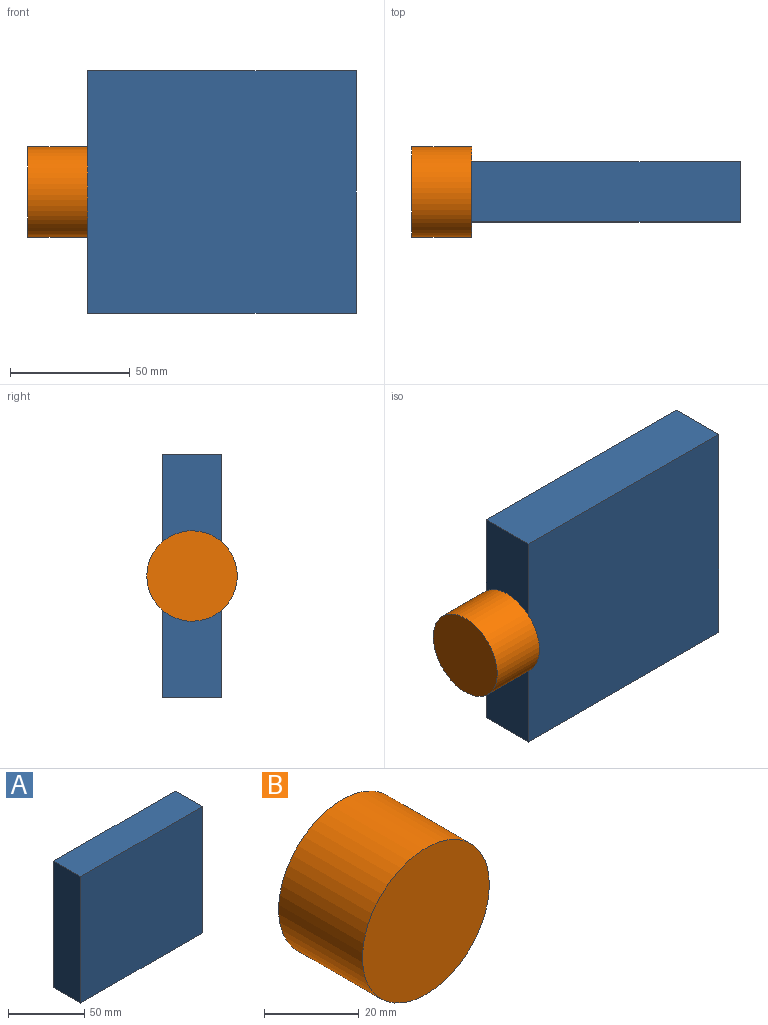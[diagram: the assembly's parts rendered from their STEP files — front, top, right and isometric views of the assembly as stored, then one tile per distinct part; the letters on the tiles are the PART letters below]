
ASSEMBLY  parts=2 mates=1
PART A: 6 faces, bbox 112.4x25x101.3 mm
  f0: plane 101.3x25mm, normal (1,0,0), area 2532.4mm2, adj f1,f3,f4,f5
  f1: plane 112.36x25mm, normal (0,0,1), area 2808.9mm2, adj f0,f2,f4,f5
  f2: plane 101.3x25mm, normal (-1,0,0), area 2532.4mm2, adj f1,f3,f4,f5
  f3: plane 112.36x25mm, normal (0,0,-1), area 2808.9mm2, adj f0,f2,f4,f5
  f4: plane 112.36x101.3mm, normal (0,-1,0), area 11381.1mm2, adj f0,f1,f2,f3
  f5: plane 112.36x101.3mm, normal (0,1,0), area 11381.1mm2, adj f0,f1,f2,f3
PART B: 3 faces, bbox 37.8x25x37.8 mm
  f0: cylinder r=18.9mm len=37.79mm, axis (0,1,0), area 2968.3mm2, adj f1,f2
  f1: plane 37.79x37.79mm, normal (0,-1,0), area 1121.8mm2, adj f0
  f2: plane 37.79x37.79mm, normal (0,1,0), area 1121.8mm2, adj f0
PLACE A at identity fixed
PLACE B rot(axis=(0.71,0.71,0),180deg) t=(-31.18,-12.5,0)mm
MATE fastened B.f0 <-> A.f2  axis (1,0,0) through (-56.18,-12.5,0)mm
